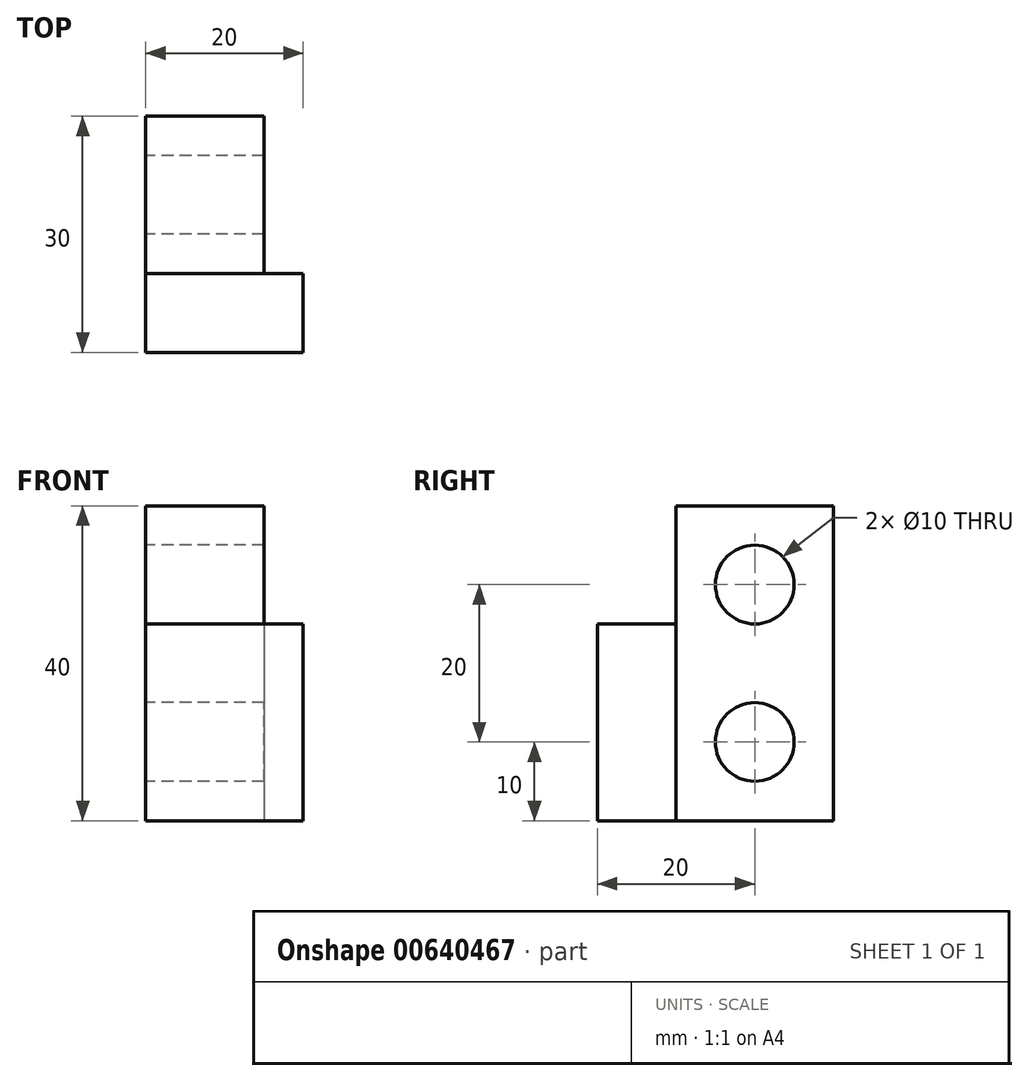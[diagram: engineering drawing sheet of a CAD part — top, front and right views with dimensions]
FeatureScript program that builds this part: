
annotation { "Feature Type Name" : "Feature", "Feature Type Description" : "" }
export const myFeature = defineFeature(function(context is Context, id is Id, definition is map)
    precondition{}
    {
        {
            var Q0;
            Q0=qCreatedBy(makeId("Right.planeOp"),FACE);
            var sketch = newSketch(context, id + "F0", { "sketchPlane" : qUnion([Q0])});
            skLineSegment(sketch, "E0.bottom", {"start": v(-10, 0) * mm, "end": v(10, 0) * mm});
            skLineSegment(sketch, "E0.top", {"start": v(-10, -40) * mm, "end": v(10, -40) * mm});
            skLineSegment(sketch, "E0.left", {"start": v(-10, 0) * mm, "end": v(-10, -40) * mm});
            skLineSegment(sketch, "E0.right", {"start": v(10, 0) * mm, "end": v(10, -40) * mm});
            skPoint(sketch, "E0.middle", {"position": v(0, -20) * mm});
            skLineSegment(sketch, "E1.bottom", {"start": v(-10, -40) * mm, "end": v(-20, -40) * mm});
            skLineSegment(sketch, "E1.top", {"start": v(-10, -15) * mm, "end": v(-20, -15) * mm});
            skLineSegment(sketch, "E1.left", {"start": v(-10, -40) * mm, "end": v(-10, -15) * mm});
            skLineSegment(sketch, "E1.right", {"start": v(-20, -40) * mm, "end": v(-20, -15) * mm});
            skCircle(sketch, "E2", {"center": v(0, -10) * mm, "radius": 5 * mm});
            skCircle(sketch, "E3", {"center": v(0, -30) * mm, "radius": 5 * mm});
            skPoint(sketch, "E3.first.point", {"position": v(-4.5, -27.81) * mm});
            skPoint(sketch, "E3.second.point", {"position": v(2.63, -34.25) * mm});
            skPoint(sketch, "E3.third.point", {"position": v(-4.37, -32.44) * mm});
            skLineSegment(sketch, "E4", {"start": v(0, 9.83) * mm, "end": v(0, -41.12) * mm, "construction": true});
            skSolve(sketch);
        }
        {
            var Q0;
            Q0=makeQuery(id+"F0.imprint","IMPRINT",FACE,{"disambiguationData":[TD([[makeQuery(id+"F0.imprint","IMPRINT",EDGE,{"derivedFrom":sQuery(id+"F0.wireOp",EDGE,"E0.bottom")}),-1.0]])]});
            extrude(context, id + "F1", {"entities" : qUnion([Q0]), "depth" : 15 * mm, "offsetDistance" : 25 * mm});
        }
        {
            var Q0;
            Q0=makeQuery(id+"F0.imprint","IMPRINT",FACE,{"disambiguationData":[TD([[makeQuery(id+"F0.imprint","IMPRINT",EDGE,{"derivedFrom":sQuery(id+"F0.wireOp",EDGE,"E1.bottom")}),-1.0]])]});
            extrude(context, id + "F2", {"entities" : qUnion([Q0]), "depth" : 20 * mm, "offsetDistance" : 25 * mm});
        }
    });
